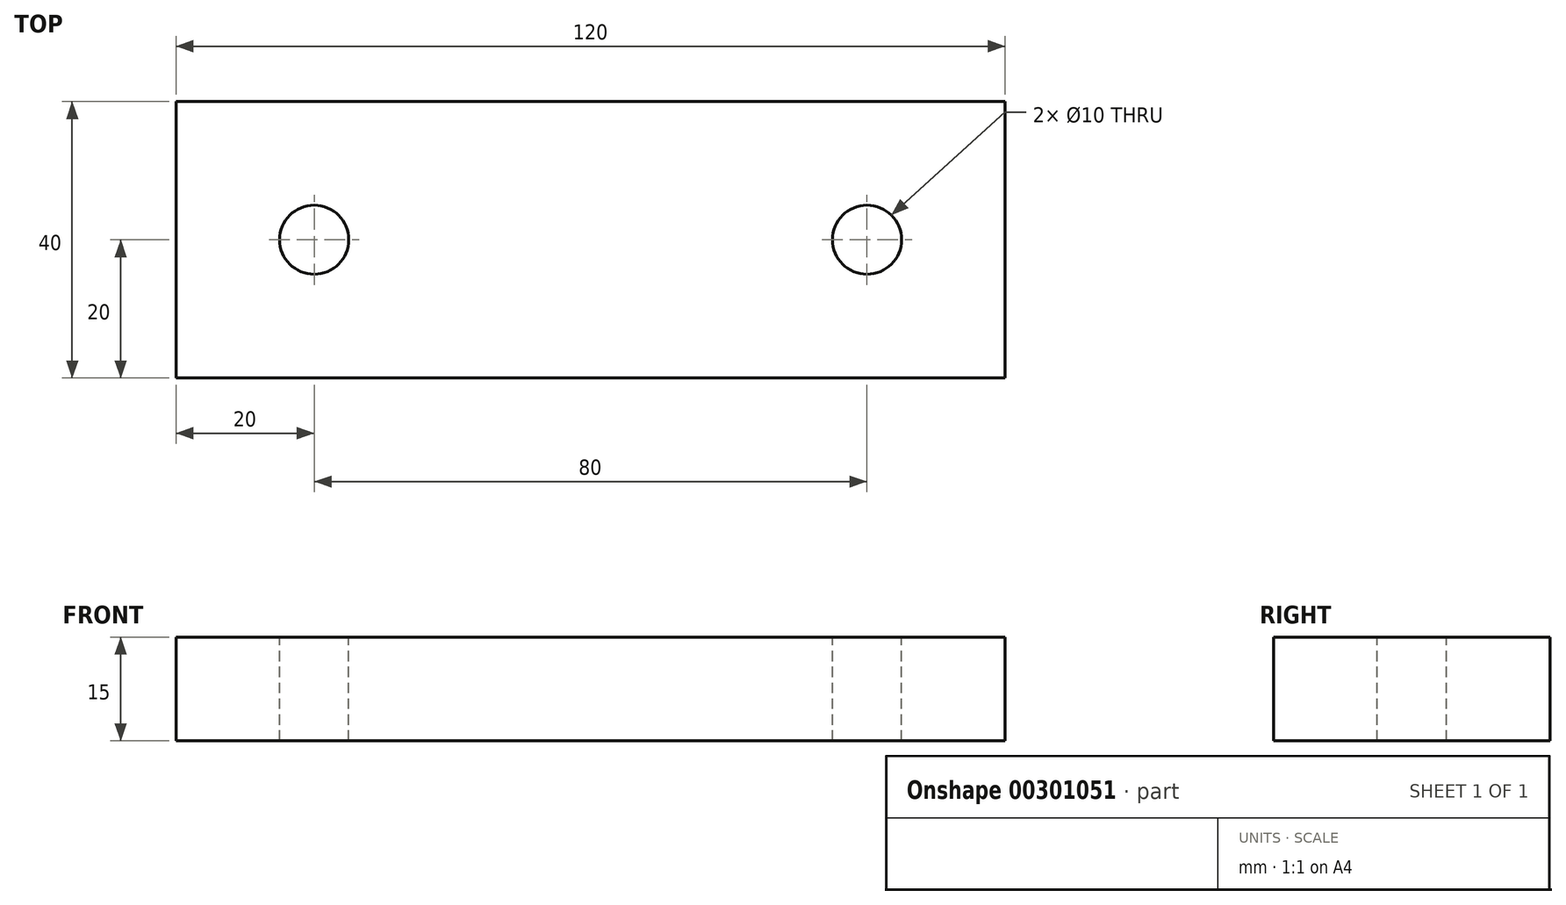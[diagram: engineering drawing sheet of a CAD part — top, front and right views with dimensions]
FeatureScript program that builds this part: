
annotation { "Feature Type Name" : "Feature", "Feature Type Description" : "" }
export const myFeature = defineFeature(function(context is Context, id is Id, definition is map)
    precondition{}
    {
        {
            var Q0;
            Q0=qCreatedBy(makeId("Front.planeOp"),FACE);
            var sketch = newSketch(context, id + "F0", { "sketchPlane" : qUnion([Q0])});
            skLineSegment(sketch, "E0.bottom", {"start": v(0, 0) * mm, "end": v(120, 0) * mm});
            skLineSegment(sketch, "E0.top", {"start": v(0, 15) * mm, "end": v(120, 15) * mm});
            skLineSegment(sketch, "E0.left", {"start": v(0, 0) * mm, "end": v(0, 15) * mm});
            skLineSegment(sketch, "E0.right", {"start": v(120, 0) * mm, "end": v(120, 15) * mm});
            skSolve(sketch);
        }
        {
            var Q0;
            Q0 = qSketchRegion(id + "F0", true);
            extrude(context, id + "F1", {"entities" : qUnion([Q0]), "endBound" : BoundingType.SYMMETRIC, "depth" : 40 * mm});
        }
        {
            var Q0;
            Q0=makeQuery(id+"F1.opExtrude","SWEPT_FACE",FACE,{"disambiguationData":[OSD([sQuery(id+"F0.wireOp",EDGE,"E0.top")])]});
            var sketch = newSketch(context, id + "F2", { "sketchPlane" : qUnion([Q0])});
            skCircle(sketch, "E1", {"center": v(20, 0) * mm, "radius": 5 * mm});
            skCircle(sketch, "E2", {"center": v(100, 0) * mm, "radius": 5 * mm});
            skSolve(sketch);
        }
        {
            var Q0;
            Q0 = qSketchRegion(id + "F2", true);
            extrude(context, id + "F3", {"entities" : qUnion([Q0]), "operationType" : NewBodyOperationType.REMOVE, "endBound" : BoundingType.THROUGH_ALL, "oppositeDirection" : true, "depth" : 25 * mm});
        }
    });
